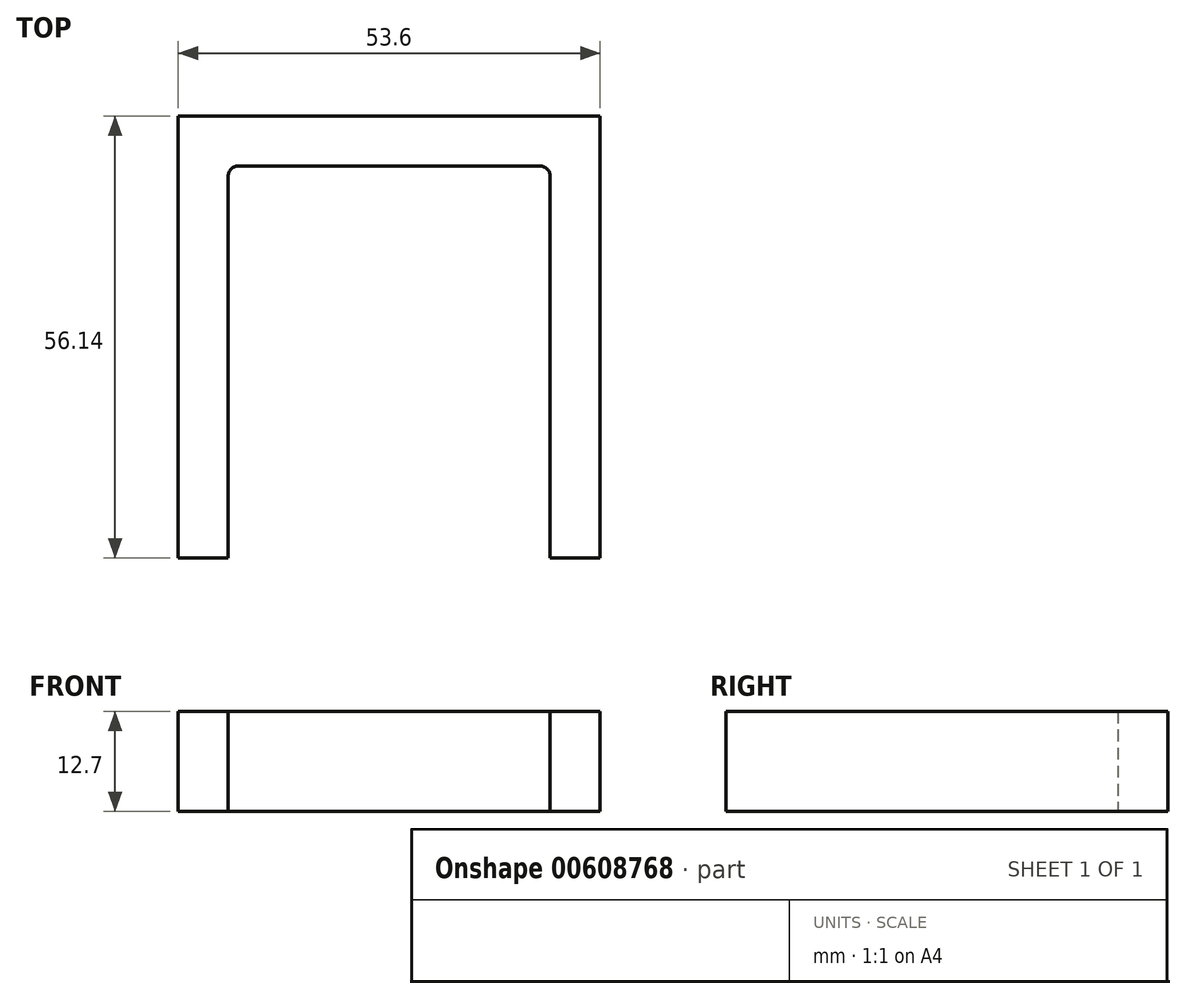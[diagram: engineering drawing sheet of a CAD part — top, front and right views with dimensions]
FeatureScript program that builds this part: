
annotation { "Feature Type Name" : "Feature", "Feature Type Description" : "" }
export const myFeature = defineFeature(function(context is Context, id is Id, definition is map)
    precondition{}
    {
        {
            var Q0;
            Q0=qCreatedBy(makeId("Top.planeOp"),FACE);
            var sketch = newSketch(context, id + "F0", { "sketchPlane" : qUnion([Q0])});
            skLineSegment(sketch, "E0.bottom", {"start": v(20.45, -20.45) * mm, "end": v(-20.45, -20.45) * mm});
            skLineSegment(sketch, "E0.top", {"start": v(20.45, 20.45) * mm, "end": v(-20.45, 20.45) * mm});
            skLineSegment(sketch, "E0.left", {"start": v(20.45, -20.45) * mm, "end": v(20.45, 20.45) * mm});
            skLineSegment(sketch, "E0.right", {"start": v(-20.45, -20.45) * mm, "end": v(-20.45, 20.45) * mm});
            skPoint(sketch, "E0.middle", {"position": v(0, 0) * mm});
            skLineSegment(sketch, "E1", {"start": v(20.45, -20.45) * mm, "end": v(18.42, -20.45) * mm});
            skLineSegment(sketch, "E2", {"start": v(18.42, -20.45) * mm, "end": v(18.42, -25.53) * mm});
            skLineSegment(sketch, "E3", {"start": v(20.45, -20.45) * mm, "end": v(20.45, -29.34) * mm});
            skLineSegment(sketch, "E4", {"start": v(20.45, -29.34) * mm, "end": v(18.42, -25.53) * mm});
            skLineSegment(sketch, "E5", {"start": v(-20.45, -20.45) * mm, "end": v(-18.42, -20.45) * mm});
            skLineSegment(sketch, "E6", {"start": v(-18.42, -20.45) * mm, "end": v(-18.42, -25.53) * mm});
            skLineSegment(sketch, "E7", {"start": v(-20.45, -20.45) * mm, "end": v(-20.45, -29.34) * mm});
            skLineSegment(sketch, "E8", {"start": v(-18.42, -25.53) * mm, "end": v(-20.45, -29.34) * mm});
            skLineSegment(sketch, "E9", {"start": v(-20.45, -29.34) * mm, "end": v(-26.8, -29.34) * mm});
            skLineSegment(sketch, "E10", {"start": v(-26.8, -29.34) * mm, "end": v(-26.8, 20.45) * mm});
            skLineSegment(sketch, "E11", {"start": v(-26.8, 20.45) * mm, "end": v(-26.8, 26.8) * mm});
            skLineSegment(sketch, "E12", {"start": v(20.45, -29.34) * mm, "end": v(26.8, -29.34) * mm});
            skLineSegment(sketch, "E13", {"start": v(26.8, -29.34) * mm, "end": v(26.8, 26.8) * mm});
            skLineSegment(sketch, "E14", {"start": v(26.8, 26.8) * mm, "end": v(-26.8, 26.8) * mm});
            skSolve(sketch);
        }
        {
            var Q0;
            Q0=makeQuery(id+"F0.imprint","IMPRINT",FACE,{"disambiguationData":[TD([[makeQuery(id+"F0.imprint","IMPRINT",EDGE,{"derivedFrom":sQuery(id+"F0.wireOp",EDGE,"E0.top")}),-1.0]])]});
            var Q1;
            Q1=makeQuery(id+"F0.imprint","IMPRINT",FACE,{"disambiguationData":[TD([[makeQuery(id+"F0.imprint","IMPRINT",EDGE,{"derivedFrom":sQuery(id+"F0.wireOp",EDGE,"E5")}),-1.0]])]});
            var Q2;
            Q2=makeQuery(id+"F0.imprint","IMPRINT",FACE,{"disambiguationData":[TD([[makeQuery(id+"F0.imprint","IMPRINT",EDGE,{"derivedFrom":sQuery(id+"F0.wireOp",EDGE,"E1")}),1.0]])]});
            extrude(context, id + "F1", {"entities" : qUnion([Q0, Q1, Q2]), "depth" : 12.7 * mm, "offsetDistance" : 25.4 * mm});
        }
        {
            var Q0;
            Q0=makeQuery(id+"F1.opExtrude","SWEPT_EDGE",EDGE,{"disambiguationData":[OSD([sQuery(id+"F0.wireOp",EDGE,"E0.top"),sQuery(id+"F0.wireOp",EDGE,"E0.right")])]});
            var Q1;
            Q1=makeQuery(id+"F1.opExtrude","SWEPT_EDGE",EDGE,{"disambiguationData":[OSD([sQuery(id+"F0.wireOp",EDGE,"E0.top"),sQuery(id+"F0.wireOp",EDGE,"E0.left")])]});
            var Q2;
            Q2=makeQuery(id+"F1.opExtrude","SWEPT_EDGE",EDGE,{"disambiguationData":[OSD([sQuery(id+"F0.wireOp",EDGE,"E0.right"),sQuery(id+"F0.wireOp",EDGE,"E5"),sQuery(id+"F0.wireOp",EDGE,"E7")])]});
            var Q3;
            Q3=makeQuery(id+"F1.opExtrude","SWEPT_EDGE",EDGE,{"disambiguationData":[OSD([sQuery(id+"F0.wireOp",EDGE,"E0.left"),sQuery(id+"F0.wireOp",EDGE,"E1"),sQuery(id+"F0.wireOp",EDGE,"E3")])]});
            fillet(context, id + "F2", {"entities" : qUnion([Q0, Q1, Q2, Q3]), "radius" : 1.27 * mm, "tangentPropagation" : true, "allowEdgeOverflow" : false});
        }
    });
